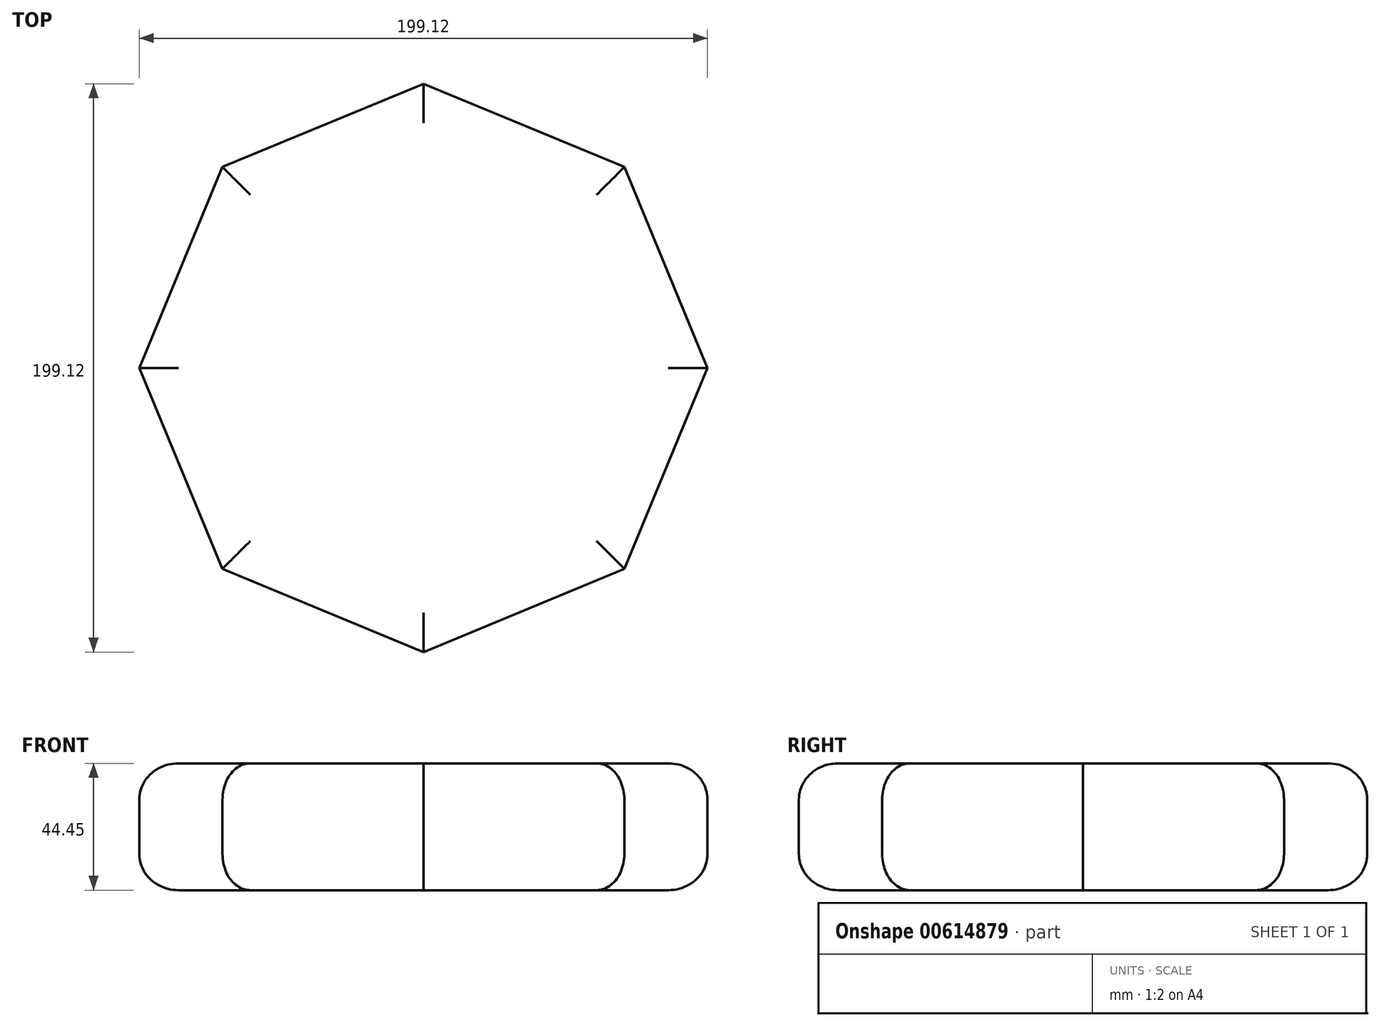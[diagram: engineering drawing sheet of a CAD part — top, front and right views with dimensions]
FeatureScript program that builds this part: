
annotation { "Feature Type Name" : "Feature", "Feature Type Description" : "" }
export const myFeature = defineFeature(function(context is Context, id is Id, definition is map)
    precondition{}
    {
        {
            var Q0;
            Q0=qCreatedBy(makeId("Top.planeOp"),FACE);
            var sketch = newSketch(context, id + "F0", { "sketchPlane" : qUnion([Q0])});
            skCircle(sketch, "E0.cCircle", {"center": v(0, 0) * mm, "radius": 91.98 * mm, "construction": true});
            skLineSegment(sketch, "E0.0", {"start": v(99.56, 0) * mm, "end": v(70.4, -70.4) * mm});
            skLineSegment(sketch, "E0.1", {"start": v(70.4, -70.4) * mm, "end": v(0, -99.56) * mm});
            skLineSegment(sketch, "E0.2", {"start": v(0, -99.56) * mm, "end": v(-70.4, -70.4) * mm});
            skLineSegment(sketch, "E0.3", {"start": v(-70.4, -70.4) * mm, "end": v(-99.56, 0) * mm});
            skLineSegment(sketch, "E0.4", {"start": v(-99.56, 0) * mm, "end": v(-70.4, 70.4) * mm});
            skLineSegment(sketch, "E0.5", {"start": v(-70.4, 70.4) * mm, "end": v(0, 99.56) * mm});
            skLineSegment(sketch, "E0.6", {"start": v(0, 99.56) * mm, "end": v(70.4, 70.4) * mm});
            skLineSegment(sketch, "E0.7", {"start": v(70.4, 70.4) * mm, "end": v(99.56, 0) * mm});
            skPoint(sketch, "E0.0.midPoint", {"position": v(84.98, -35.2) * mm});
            skSolve(sketch);
        }
        {
            var Q0;
            Q0=qSketchRegion(id+"F0",true);
            extrude(context, id + "F1", {"entities" : qUnion([Q0]), "depth" : 44.45 * mm, "offsetDistance" : 25.4 * mm});
        }
        {
            var Q0;
            Q0=makeQuery(id+"F1.opExtrude","CAP_EDGE",EDGE,{"disambiguationData":[OSD([sQuery(id+"F0.wireOp",EDGE,"E0.3")])],"isStart":false});
            var Q1;
            Q1=makeQuery(id+"F1.opExtrude","CAP_EDGE",EDGE,{"disambiguationData":[OSD([sQuery(id+"F0.wireOp",EDGE,"E0.2")])],"isStart":false});
            var Q2;
            Q2=makeQuery(id+"F1.opExtrude","CAP_EDGE",EDGE,{"disambiguationData":[OSD([sQuery(id+"F0.wireOp",EDGE,"E0.1")])],"isStart":false});
            var Q3;
            Q3=makeQuery(id+"F1.opExtrude","CAP_EDGE",EDGE,{"disambiguationData":[OSD([sQuery(id+"F0.wireOp",EDGE,"E0.0")])],"isStart":false});
            var Q4;
            Q4=makeQuery(id+"F1.opExtrude","CAP_EDGE",EDGE,{"disambiguationData":[OSD([sQuery(id+"F0.wireOp",EDGE,"E0.7")])],"isStart":false});
            var Q5;
            Q5=makeQuery(id+"F1.opExtrude","CAP_EDGE",EDGE,{"disambiguationData":[OSD([sQuery(id+"F0.wireOp",EDGE,"E0.6")])],"isStart":false});
            var Q6;
            Q6=makeQuery(id+"F1.opExtrude","CAP_EDGE",EDGE,{"disambiguationData":[OSD([sQuery(id+"F0.wireOp",EDGE,"E0.5")])],"isStart":false});
            var Q7;
            Q7=makeQuery(id+"F1.opExtrude","CAP_EDGE",EDGE,{"disambiguationData":[OSD([sQuery(id+"F0.wireOp",EDGE,"E0.4")])],"isStart":false});
            var Q8;
            Q8=makeQuery(id+"F1.opExtrude","CAP_EDGE",EDGE,{"disambiguationData":[OSD([sQuery(id+"F0.wireOp",EDGE,"E0.1")])],"isStart":true});
            var Q9;
            Q9=makeQuery(id+"F1.opExtrude","CAP_EDGE",EDGE,{"disambiguationData":[OSD([sQuery(id+"F0.wireOp",EDGE,"E0.2")])],"isStart":true});
            var Q10;
            Q10=makeQuery(id+"F1.opExtrude","CAP_EDGE",EDGE,{"disambiguationData":[OSD([sQuery(id+"F0.wireOp",EDGE,"E0.0")])],"isStart":true});
            var Q11;
            Q11=makeQuery(id+"F1.opExtrude","CAP_EDGE",EDGE,{"disambiguationData":[OSD([sQuery(id+"F0.wireOp",EDGE,"E0.7")])],"isStart":true});
            var Q12;
            Q12=makeQuery(id+"F1.opExtrude","CAP_EDGE",EDGE,{"disambiguationData":[OSD([sQuery(id+"F0.wireOp",EDGE,"E0.3")])],"isStart":true});
            var Q13;
            Q13=makeQuery(id+"F1.opExtrude","CAP_EDGE",EDGE,{"disambiguationData":[OSD([sQuery(id+"F0.wireOp",EDGE,"E0.6")])],"isStart":true});
            var Q14;
            Q14=makeQuery(id+"F1.opExtrude","CAP_EDGE",EDGE,{"disambiguationData":[OSD([sQuery(id+"F0.wireOp",EDGE,"E0.5")])],"isStart":true});
            var Q15;
            Q15=makeQuery(id+"F1.opExtrude","CAP_EDGE",EDGE,{"disambiguationData":[OSD([sQuery(id+"F0.wireOp",EDGE,"E0.4")])],"isStart":true});
            fillet(context, id + "F2", {"entities" : qUnion([Q0, Q1, Q2, Q3, Q4, Q5, Q6, Q7, Q8, Q9, Q10, Q11, Q12, Q13, Q14, Q15]), "radius" : 12.7 * mm, "tangentPropagation" : true, "allowEdgeOverflow" : false});
        }
    });
